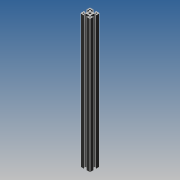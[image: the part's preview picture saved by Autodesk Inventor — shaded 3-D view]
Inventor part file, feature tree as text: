
AUTODESK INVENTOR PART (.ipt)
format: ipt  version: 2019 (Build 230136000, 136)  size: 238,592 bytes
history: native  units: mm
features: extrude x1, sketch x1, projected_geometry x1, other x1
ambient origin geometry x8: Origin, YZ Plane, XZ Plane, XY Plane, X Axis, Y Axis, Z Axis, Center Point
bodies: Solid1 (feature_tree)
feature tree (4):
  extrude  "Extrusion1"  [1 undecoded]
  sketch  "Sketch1"  dims[d0=125.0mm d1=0.0mm]
  projected_geometry  "Projected Loop1"
  parser-record x1  (decoder bookkeeping rows leaked as tree rows — omitted from the tree; the rows remain in map.json)
note: 1 required parameter value undecoded (feature->parameter linkage not recoverable at this tier; creation-order binding heuristic only, values carry confidence <= 0.55)
